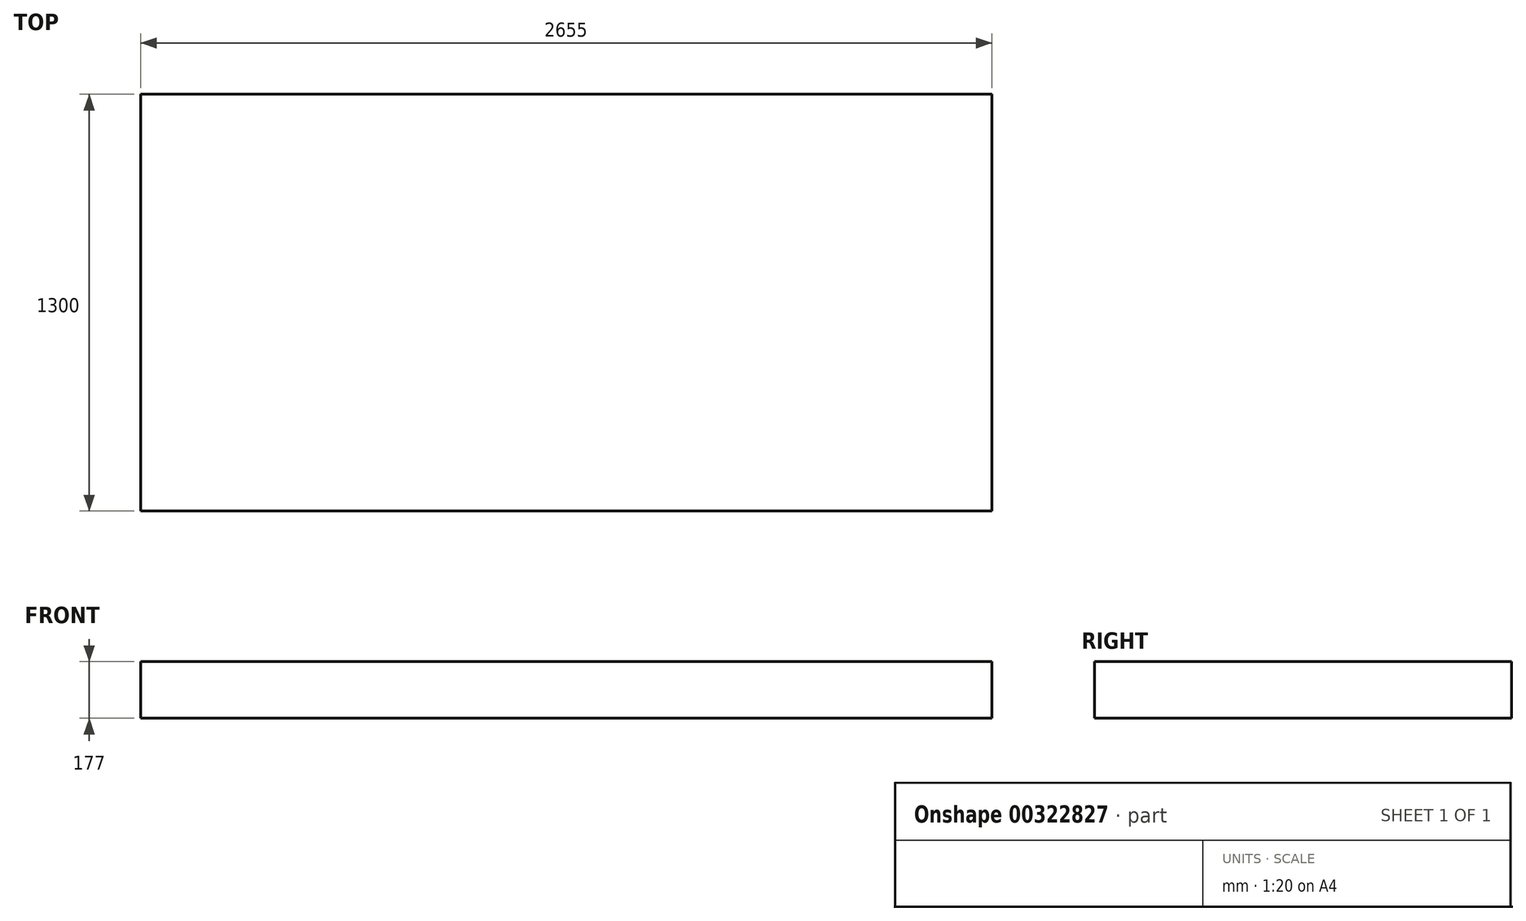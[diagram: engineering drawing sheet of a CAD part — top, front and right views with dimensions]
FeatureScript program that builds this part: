
annotation { "Feature Type Name" : "Feature", "Feature Type Description" : "" }
export const myFeature = defineFeature(function(context is Context, id is Id, definition is map)
    precondition{}
    {
        {
            var Q0;
            Q0=qCreatedBy(makeId("Top.planeOp"),FACE);
            var sketch = newSketch(context, id + "F0", { "sketchPlane" : qUnion([Q0])});
            skLineSegment(sketch, "E0.bottom", {"start": v(1327.5, -650) * mm, "end": v(-1327.5, -650) * mm});
            skLineSegment(sketch, "E0.top", {"start": v(1327.5, 650) * mm, "end": v(-1327.5, 650) * mm});
            skLineSegment(sketch, "E0.left", {"start": v(1327.5, -650) * mm, "end": v(1327.5, 650) * mm});
            skLineSegment(sketch, "E0.right", {"start": v(-1327.5, -650) * mm, "end": v(-1327.5, 650) * mm});
            skPoint(sketch, "E0.middle", {"position": v(0, 0) * mm});
            skLineSegment(sketch, "E1.bottom", {"start": v(-1327.5, 650) * mm, "end": v(-1227.5, 650) * mm});
            skLineSegment(sketch, "E1.top", {"start": v(-1327.5, -650) * mm, "end": v(-1227.5, -650) * mm});
            skLineSegment(sketch, "E1.left", {"start": v(-1327.5, 650) * mm, "end": v(-1327.5, -650) * mm});
            skLineSegment(sketch, "E1.right", {"start": v(-1227.5, 650) * mm, "end": v(-1227.5, -650) * mm});
            skLineSegment(sketch, "E2.bottom", {"start": v(1327.5, 650) * mm, "end": v(1237.5, 650) * mm});
            skLineSegment(sketch, "E2.top", {"start": v(1327.5, -650) * mm, "end": v(1237.5, -650) * mm});
            skLineSegment(sketch, "E2.left", {"start": v(1327.5, 650) * mm, "end": v(1327.5, -650) * mm});
            skLineSegment(sketch, "E2.right", {"start": v(1237.5, 650) * mm, "end": v(1237.5, -650) * mm});
            skSolve(sketch);
        }
        {
            var Q0;
            Q0=makeQuery(id+"F0.imprint","IMPRINT",FACE,{"disambiguationData":[TD([[makeQuery(id+"F0.imprint","IMPRINT",EDGE,{"derivedFrom":sQuery(id+"F0.wireOp",EDGE,"E0.bottom")}),-1.0]])]});
            var Q1;
            Q1=makeQuery(id+"F0.imprint","IMPRINT",FACE,{"disambiguationData":[TD([[makeQuery(id+"F0.imprint","IMPRINT",EDGE,{"derivedFrom":sQuery(id+"F0.wireOp",EDGE,"E1.bottom")}),-1.0]])]});
            var Q2;
            Q2=makeQuery(id+"F0.imprint","IMPRINT",FACE,{"disambiguationData":[TD([[makeQuery(id+"F0.imprint","IMPRINT",EDGE,{"derivedFrom":sQuery(id+"F0.wireOp",EDGE,"E2.bottom")}),1.0]])]});
            extrude(context, id + "F1", {"entities" : qUnion([Q0, Q1, Q2]), "oppositeDirection" : true, "depth" : 177 * mm});
        }
    });
